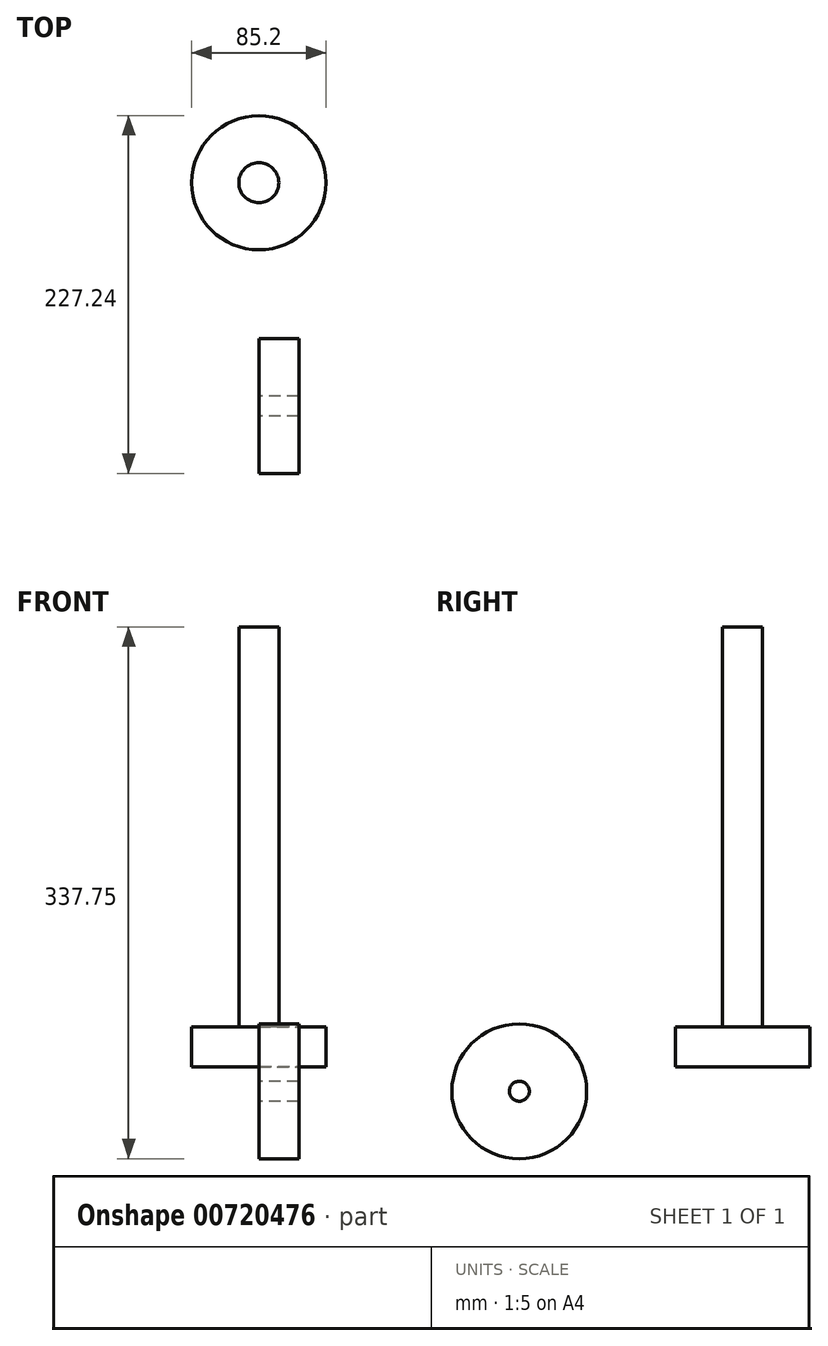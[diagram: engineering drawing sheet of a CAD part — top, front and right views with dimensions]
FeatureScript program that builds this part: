
annotation { "Feature Type Name" : "Feature", "Feature Type Description" : "" }
export const myFeature = defineFeature(function(context is Context, id is Id, definition is map)
    precondition{}
    {
        {
            var Q0;
            Q0=qCreatedBy(makeId("Top.planeOp"),FACE);
            var sketch = newSketch(context, id + "F0", { "sketchPlane" : qUnion([Q0])});
            skCircle(sketch, "E0", {"center": v(0, 0) * mm, "radius": 42.6 * mm});
            skSolve(sketch);
        }
        {
            var Q0;
            Q0=makeQuery(id+"F0.imprint","IMPRINT",FACE,{"disambiguationData":[TD([[makeQuery(id+"F0.imprint","IMPRINT",EDGE,{"derivedFrom":sQuery(id+"F0.wireOp",EDGE,"E0")}),1.0]])]});
            extrude(context, id + "F1", {"entities" : qUnion([Q0]), "depth" : 25.4 * mm, "offsetDistance" : 25.4 * mm});
        }
        {
            var Q0;
            Q0=qCreatedBy(makeId("Right.planeOp"),FACE);
            var sketch = newSketch(context, id + "F2", { "sketchPlane" : qUnion([Q0])});
            skCircle(sketch, "E1", {"center": v(-141.82, -15.54) * mm, "radius": 42.82 * mm});
            skSolve(sketch);
        }
        {
            var Q0;
            Q0=makeQuery(id+"F2.imprint","IMPRINT",FACE,{"disambiguationData":[TD([[makeQuery(id+"F2.imprint","IMPRINT",EDGE,{"derivedFrom":sQuery(id+"F2.wireOp",EDGE,"E1")}),1.0]])]});
            extrude(context, id + "F3", {"entities" : qUnion([Q0]), "depth" : 25.4 * mm, "offsetDistance" : 25.4 * mm});
        }
        {
            var Q0;
            Q0=makeQuery(id+"F1.opExtrude","CAP_FACE",FACE,{"disambiguationData":[OSD([sQuery(id+"F0.wireOp",EDGE,"E0")])],"isStart":false});
            var sketch = newSketch(context, id + "F4", { "sketchPlane" : qUnion([Q0])});
            skCircle(sketch, "E2", {"center": v(0, 0) * mm, "radius": 12.7 * mm});
            skSolve(sketch);
        }
        {
            var Q0;
            Q0=makeQuery(id+"F4.imprint","IMPRINT",FACE,{"disambiguationData":[TD([[makeQuery(id+"F4.imprint","IMPRINT",EDGE,{"derivedFrom":sQuery(id+"F4.wireOp",EDGE,"E2")}),1.0]])]});
            extrude(context, id + "F5", {"entities" : qUnion([Q0]), "operationType" : NewBodyOperationType.ADD, "depth" : 254 * mm, "offsetDistance" : 25.4 * mm});
        }
        {
            var Q0;
            Q0=makeQuery(id+"F3.opExtrude","CAP_FACE",FACE,{"disambiguationData":[OSD([sQuery(id+"F2.wireOp",EDGE,"E1")])],"isStart":true});
            var sketch = newSketch(context, id + "F6", { "sketchPlane" : qUnion([Q0])});
            skCircle(sketch, "E3", {"center": v(141.82, -15.54) * mm, "radius": 6.35 * mm});
            skSolve(sketch);
        }
        {
            var Q0;
            Q0=makeQuery(id+"F6.imprint","IMPRINT",FACE,{"disambiguationData":[TD([[makeQuery(id+"F6.imprint","IMPRINT",EDGE,{"derivedFrom":sQuery(id+"F6.wireOp",EDGE,"E3")}),1.0]])]});
            extrude(context, id + "F7", {"entities" : qUnion([Q0]), "operationType" : NewBodyOperationType.REMOVE, "oppositeDirection" : true, "depth" : 25.4 * mm, "offsetDistance" : 25.4 * mm});
        }
    });
